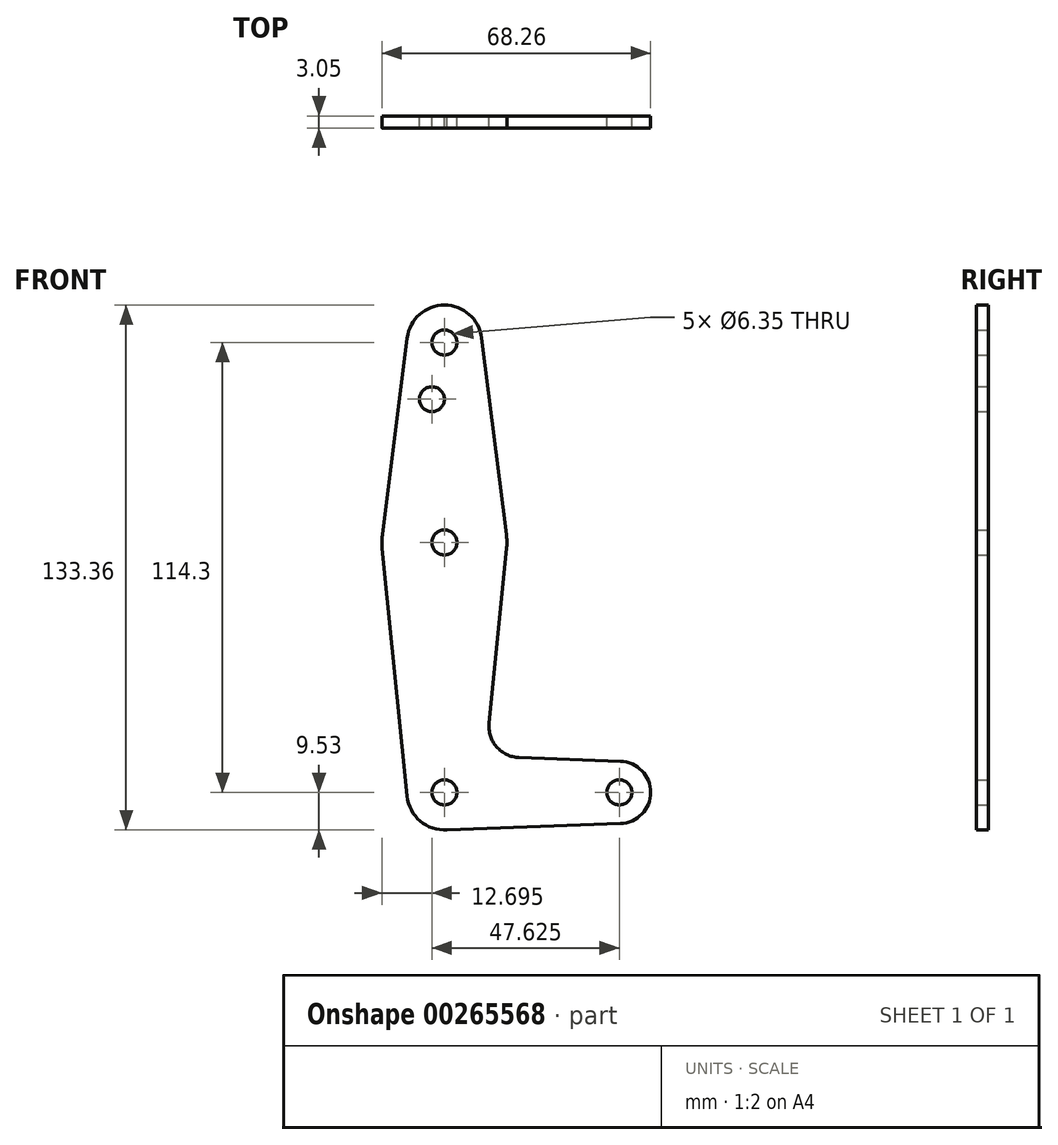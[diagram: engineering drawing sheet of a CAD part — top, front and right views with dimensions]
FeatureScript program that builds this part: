
annotation { "Feature Type Name" : "Feature", "Feature Type Description" : "" }
export const myFeature = defineFeature(function(context is Context, id is Id, definition is map)
    precondition{}
    {
        {
            var Q0;
            Q0=qCreatedBy(makeId("Front.planeOp"),FACE);
            var sketch = newSketch(context, id + "F0", { "sketchPlane" : qUnion([Q0])});
            skLineSegment(sketch, "E0", {"start": v(0, 114.3) * mm, "end": v(0, 63.5) * mm});
            skLineSegment(sketch, "E1", {"start": v(0, 63.5) * mm, "end": v(0, 0) * mm});
            skLineSegment(sketch, "E2", {"start": v(0, 0) * mm, "end": v(44.45, 0) * mm});
            skCircle(sketch, "E3", {"center": v(0, 114.3) * mm, "radius": 9.53 * mm});
            skCircle(sketch, "E4", {"center": v(0, 63.5) * mm, "radius": 15.88 * mm});
            skCircle(sketch, "E5", {"center": v(0, 0) * mm, "radius": 9.53 * mm});
            skCircle(sketch, "E6", {"center": v(44.45, 0) * mm, "radius": 7.94 * mm});
            skLineSegment(sketch, "E7", {"start": v(-9.45, 115.5) * mm, "end": v(-15.75, 65.48) * mm});
            skLineSegment(sketch, "E8", {"start": v(9.45, 115.5) * mm, "end": v(15.75, 65.48) * mm});
            skLineSegment(sketch, "E9", {"start": v(15.8, 61.91) * mm, "end": v(11.34, 17.6) * mm});
            skLineSegment(sketch, "E10", {"start": v(-15.8, 61.91) * mm, "end": v(-9.48, -0.95) * mm});
            skLineSegment(sketch, "E11", {"start": v(0, -9.52) * mm, "end": v(44.73, -7.93) * mm});
            skCircle(sketch, "E12", {"center": v(-3.17, 99.89) * mm, "radius": 3.18 * mm});
            skCircle(sketch, "E13", {"center": v(0, 114.3) * mm, "radius": 3.18 * mm});
            skCircle(sketch, "E14", {"center": v(0, 63.5) * mm, "radius": 3.18 * mm});
            skCircle(sketch, "E15", {"center": v(0, 0) * mm, "radius": 3.18 * mm});
            skCircle(sketch, "E16", {"center": v(44.45, 0) * mm, "radius": 3.18 * mm});
            skLineSegment(sketch, "E17", {"start": v(18.97, 8.85) * mm, "end": v(44.73, 7.93) * mm});
            skArc(sketch, "E18.filletArc", {"start": v(11.34, 17.6) * mm, "mid": v(13.26, 11.57) * mm, "end": v(18.97, 8.85) * mm});
            skSolve(sketch);
        }
        {
            var Q0;
            Q0 = qSketchRegion(id + "F0", true);
            var Q1;
            {var subQ0=sQuery(id+"F0.wireOp",EDGE,"E5");var subQ1=sQuery(id+"F0.wireOp",EDGE,"E1");var subQ2=makeQuery(id+"F0.imprint","INTERSECT",VERTEX,{"derivedFrom":[subQ1,subQ0]});Q1=makeQuery(id+"F0.imprint","IMPRINT",FACE,{"disambiguationData":[TD([[makeQuery(id+"F0.imprint","IMPRINT",EDGE,{"disambiguationData":[TD([[subQ2,-1.0]])],"derivedFrom":subQ1}),1.0]])]});}
            extrude(context, id + "F1", {"entities" : qUnion([Q0, Q1]), "depth" : 3.05 * mm});
        }
    });
